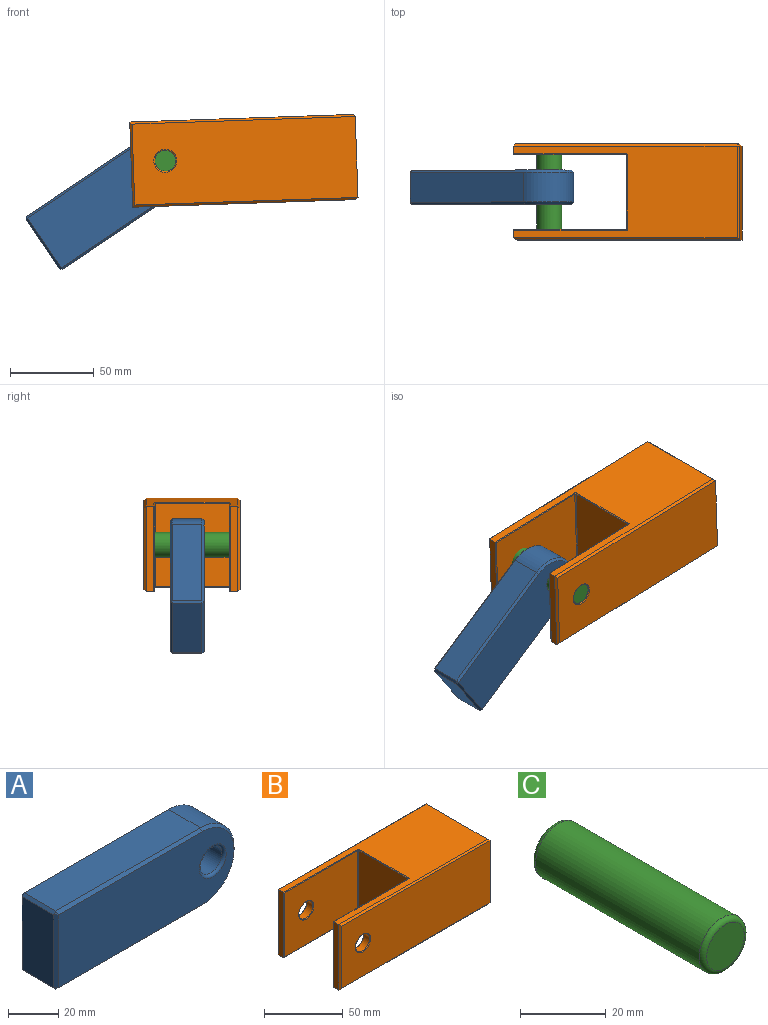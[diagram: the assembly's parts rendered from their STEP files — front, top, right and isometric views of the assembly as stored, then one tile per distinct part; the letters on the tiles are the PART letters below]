
ASSEMBLY  parts=3 mates=2
PART A: 23 faces, bbox 101.7x20.3x38.1 mm
  f0: plane 35.56x17.79mm, normal (-1,0,0), area 632.6mm2, adj f11,f15,f16,f17
  f1: plane 99.11x35.56mm, normal (0,-1,0), area 3206.4mm2, adj f6,f9,f10,f11,f12
  f2: plane 99.11x35.56mm, normal (0,1,0), area 3206.4mm2, adj f7,f16,f20,f21,f22
  f3: plane 81.33x17.79mm, normal (0,0,1), area 1447mm2, adj f8,f10,f15,f20
  f4: plane 81.33x17.79mm, normal (0,0,-1), area 1447mm2, adj f8,f12,f17,f21
  f5: cylinder r=6.35mm len=17.79mm, axis (0,1,0), area 709.8mm2, adj f6,f7
  f6: torus R=7.62mm, axis (0,1,0), area 85.4mm2, adj f1,f5
  f7: torus R=7.62mm, axis (0,1,0), area 85.4mm2, adj f2,f5
  f8: cylinder r=19.05mm len=38.1mm, axis (0,-1,0), area 1064.7mm2, adj f3,f4,f9,f22
  f9: cone r=17.78mm half-angle=45deg, axis (0,1,0), area 103.9mm2, adj f1,f8,f10,f12
  f10: plane 81.33x1.27mm, normal (0,-0.71,0.71), area 146.1mm2, adj f1,f3,f9,f13
  f11: plane 35.56x1.27mm, normal (-0.71,-0.71,0), area 63.9mm2, adj f0,f1,f13,f14
  f12: plane 81.33x1.27mm, normal (0,-0.71,-0.71), area 146.1mm2, adj f1,f4,f9,f14
  f13: plane 1.27x1.27mm, normal (-0.58,-0.58,0.58), area 1.4mm2, adj f10,f11,f15
  f14: plane 1.27x1.27mm, normal (-0.58,-0.58,-0.58), area 1.4mm2, adj f11,f12,f17
  f15: plane 17.79x1.27mm, normal (-0.71,0,0.71), area 32mm2, adj f0,f3,f13,f18
  f16: plane 35.56x1.27mm, normal (-0.71,0.71,0), area 63.9mm2, adj f0,f2,f18,f19
  f17: plane 17.79x1.27mm, normal (-0.71,0,-0.71), area 32mm2, adj f0,f4,f14,f19
  f18: plane 1.27x1.27mm, normal (-0.58,0.58,0.58), area 1.4mm2, adj f15,f16,f20
  f19: plane 1.27x1.27mm, normal (-0.58,0.58,-0.58), area 1.4mm2, adj f16,f17,f21
  f20: plane 81.33x1.27mm, normal (0,0.71,0.71), area 146.1mm2, adj f2,f3,f18,f22
  f21: plane 81.33x1.27mm, normal (0,0.71,-0.71), area 146.1mm2, adj f2,f4,f19,f22
  f22: cone r=17.78mm half-angle=45deg, axis (0,-1,0), area 103.9mm2, adj f2,f8,f20,f21
PART B: 38 faces, bbox 134.4x57.3x50.8 mm
  f0: plane 50.8x4.51mm, normal (-1,0,0), area 229.2mm2, adj f1,f6,f16,f27
  f1: plane 133.16x54.72mm, normal (0,0,-1), area 4192.1mm2, adj f0,f4,f12,f13,f14,f15,f30,f34
  f2: plane 55.99x48.26mm, normal (1,0,0), area 2702mm2, adj f5,f29,f33,f34
  f3: plane 131.89x48.26mm, normal (0,1,0), area 6217.4mm2, adj f26,f27,f28,f29,f30
  f4: plane 50.8x4.51mm, normal (-1,0,0), area 229.2mm2, adj f1,f6,f17,f37
  f5: plane 133.16x48.26mm, normal (0,-1,0), area 6278.6mm2, adj f2,f23,f35,f36,f37
  f6: plane 133.16x54.72mm, normal (0,0,1), area 4192.1mm2, adj f0,f4,f19,f20,f21,f22,f28,f33
  f7: plane 49.78x44.17mm, normal (-1,0,0), area 2198.9mm2, adj f9,f12,f18,f22
  f8: plane 66.2x49.78mm, normal (0,-1,0), area 3147.9mm2, adj f13,f16,f18,f19,f24
  f9: plane 66.71x49.78mm, normal (0,1,0), area 3173.2mm2, adj f7,f14,f17,f20,f25
  f10: cylinder r=6.35mm len=12.7mm, axis (0,1,0), area 210.4mm2, adj f23,f25
  f11: cylinder r=6.35mm len=12.7mm, axis (0,1,0), area 210.4mm2, adj f24,f26
  f12: cylinder r=0.51mm len=44.68mm, axis (0,-1,0), area 35.4mm2, adj f1,f7,f14,f15
  f13: cylinder r=0.51mm len=66.71mm, axis (1,0,0), area 53.1mm2, adj f1,f8,f15,f16
  f14: cylinder r=0.51mm len=67.72mm, axis (-1,0,0), area 53.6mm2, adj f1,f9,f12,f17
  f15: torus R=1.02mm, axis (0,0,1), area 0.9mm2, adj f1,f12,f13,f18
  f16: cylinder r=0.51mm len=50.8mm, axis (0,0,1), area 40.2mm2, adj f0,f8,f13,f19
  f17: cylinder r=0.51mm len=50.8mm, axis (0,0,-1), area 40.2mm2, adj f4,f9,f14,f20
  f18: cylinder r=0.51mm len=49.78mm, axis (0,0,1), area 39.7mm2, adj f7,f8,f15,f21
  f19: cylinder r=0.51mm len=66.71mm, axis (-1,0,0), area 53.1mm2, adj f6,f8,f16,f21
  f20: cylinder r=0.51mm len=67.72mm, axis (1,0,0), area 53.6mm2, adj f6,f9,f17,f22
  f21: torus R=1.02mm, axis (0,0,1), area 0.9mm2, adj f6,f18,f19,f22
  f22: cylinder r=0.51mm len=44.68mm, axis (0,1,0), area 35.4mm2, adj f6,f7,f20,f21
  f23: torus R=6.86mm, axis (0,-1,0), area 32.8mm2, adj f5,f10
  f24: torus R=6.86mm, axis (0,-1,0), area 32.8mm2, adj f8,f11
  f25: torus R=6.86mm, axis (0,-1,0), area 32.8mm2, adj f9,f10
  f26: torus R=6.86mm, axis (0,-1,0), area 32.8mm2, adj f3,f11
  f27: plane 50.8x1.27mm, normal (-0.71,0.71,0), area 89mm2, adj f0,f3,f28,f30
  f28: plane 133.16x1.27mm, normal (0,0.71,0.71), area 238mm2, adj f3,f6,f27,f31
  f29: plane 48.26x1.27mm, normal (0.71,0.71,0), area 86.7mm2, adj f2,f3,f31,f32
  f30: plane 133.16x1.27mm, normal (0,0.71,-0.71), area 238mm2, adj f1,f3,f27,f32
  f31: plane 1.27x1.27mm, normal (0.58,0.58,0.58), area 1.4mm2, adj f28,f29,f33
  f32: plane 1.27x1.27mm, normal (0.58,0.58,-0.58), area 1.4mm2, adj f29,f30,f34
  f33: plane 55.99x1.27mm, normal (0.71,0,0.71), area 99.4mm2, adj f2,f6,f31,f35
  f34: plane 55.99x1.27mm, normal (0.71,0,-0.71), area 99.4mm2, adj f1,f2,f32,f36
  f35: plane 134.43x1.27mm, normal (0,-0.71,0.71), area 239.2mm2, adj f5,f6,f33,f37
  f36: plane 134.43x1.27mm, normal (0,-0.71,-0.71), area 239.2mm2, adj f1,f5,f34,f37
  f37: plane 50.8x1.27mm, normal (-0.71,-0.71,0), area 89mm2, adj f4,f5,f35,f36
PART C: 5 faces, bbox 16.2x56.4x16.2 mm
  f0: cylinder r=7.48mm len=53.85mm, axis (0,1,0), area 2531.7mm2, adj f3,f4
  f1: plane 12.43x12.43mm, normal (0,-1,0), area 121.3mm2, adj f4
  f2: plane 12.43x12.43mm, normal (0,1,0), area 121.3mm2, adj f3
  f3: torus R=6.21mm, axis (0,-1,0), area 88mm2, adj f0,f2
  f4: torus R=6.21mm, axis (0,-1,0), area 88mm2, adj f0,f1
PLACE A rot(axis=(0,-1,0),34deg) t=(184.6,-82.4,163.82)mm
PLACE B rot(axis=(0,-1,0),2deg) t=(255.56,-95.5,177.53)mm
PLACE C rot(axis=(0,-1,0),2deg) t=(207.83,-67.23,202.95)mm
MATE cylindrical C.f0 <-> A.f5  axis (0,1,0) through (207.83,-95.43,202.95)mm
MATE fastened B.f10 <-> C.f0  axis (0,-1,0) through (207.83,-123.62,202.95)mm
